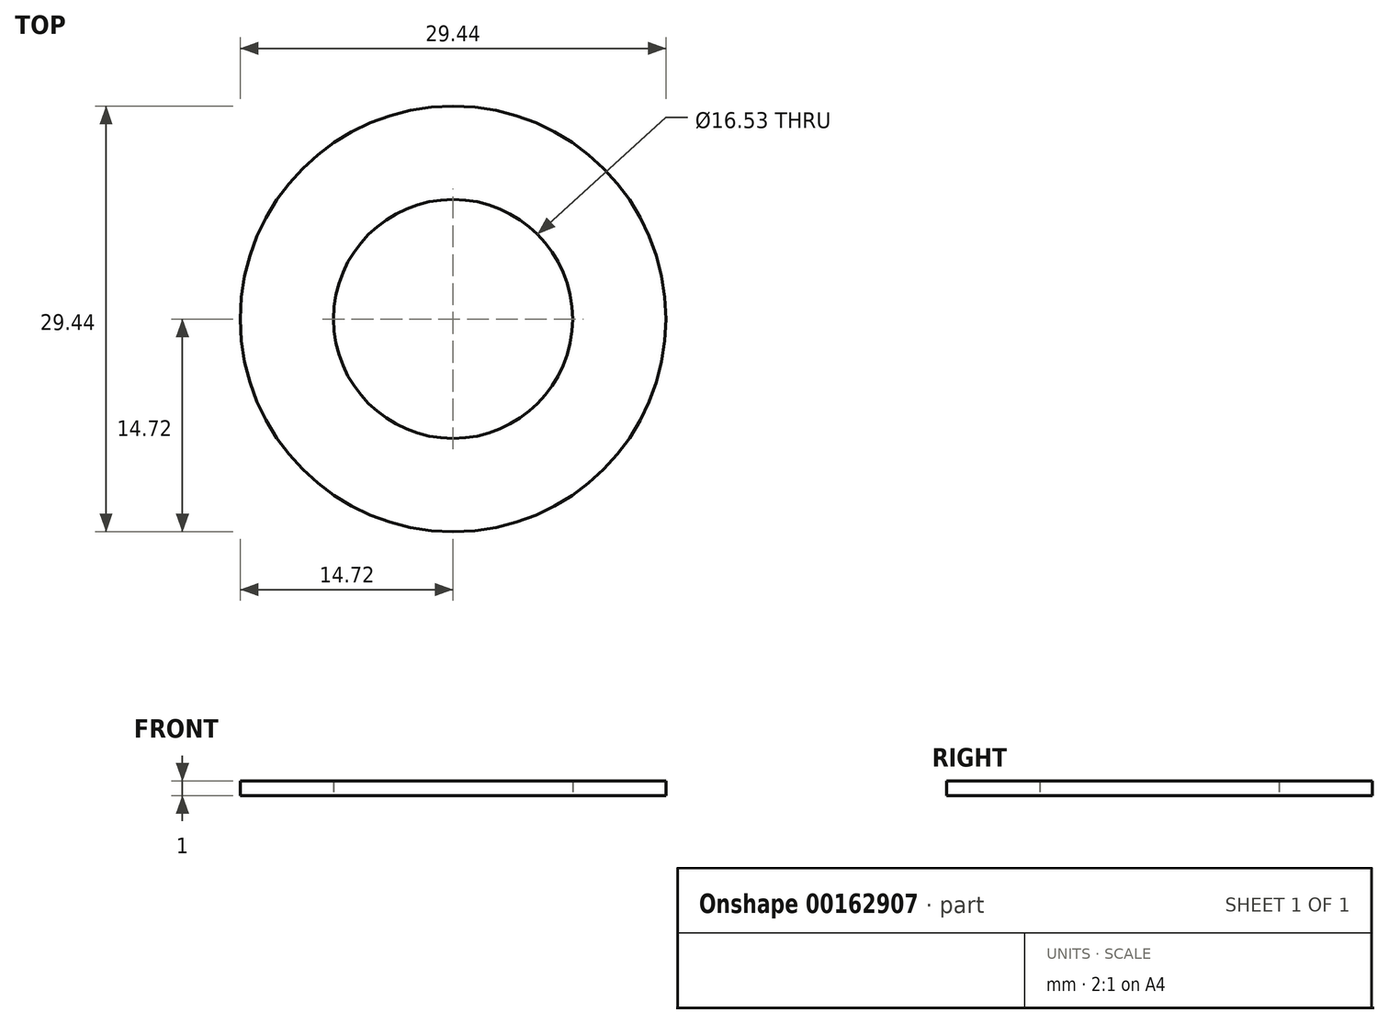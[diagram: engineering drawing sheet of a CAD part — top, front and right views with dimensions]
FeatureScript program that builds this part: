
annotation { "Feature Type Name" : "Feature", "Feature Type Description" : "" }
export const myFeature = defineFeature(function(context is Context, id is Id, definition is map)
    precondition{}
    {
        {
            var Q0;
            Q0=qCreatedBy(makeId("Top.planeOp"),FACE);
            var sketch = newSketch(context, id + "F0", { "sketchPlane" : qUnion([Q0])});
            skCircle(sketch, "E0", {"center": v(0, 0) * mm, "radius": 8.27 * mm});
            skCircle(sketch, "E1", {"center": v(0, 0) * mm, "radius": 14.72 * mm});
            skSolve(sketch);
        }
        {
            var Q0;
            Q0 = qSketchRegion(id + "F0", true);
            extrude(context, id + "F1", {"entities" : qUnion([Q0]), "depth" : 1 * mm});
        }
    });
